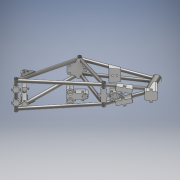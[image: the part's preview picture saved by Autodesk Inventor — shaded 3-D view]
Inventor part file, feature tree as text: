
AUTODESK INVENTOR PART (.ipt)
format: ipt  version: 2018 (Build 220112000, 112)  size: 1,251,840 bytes
history: native  units: mm
features: sketch x35, extrude x33, other x22, fillet x7, mirror x5, projected_geometry x5, plane x2, boolean_combine x2, loft x1, hole x1
ambient origin geometry x8: Origin, YZ Plane, XZ Plane, XY Plane, X Axis, Y Axis, Z Axis, Center Point
bodies: Solid1 (feature_tree), Solid2 (feature_tree), Solid3 (feature_tree), Solid16 (feature_tree), Solid17 (feature_tree), Solid21 (feature_tree)
feature tree (113):
  other  "MainFrame.ipt"
  other  "Floor"
  extrude  "Extrusion1"  Depth=10.0mm
  extrude  "Extrusion3"  Depth=18.25mm TaperAngle=0.0deg
  extrude  "Extrusion2"  Depth=4.0mm
  mirror  "Mirror1"
  extrude  "Extrusion5"  Depth=4.0mm TaperAngle=0.0deg
  extrude  "Extrusion6"  Depth=87.0mm TaperAngle=0.0deg
  extrude  "Extrusion7"  Depth=17.5mm TaperAngle=0.0deg
  extrude  "Extrusion8"  Depth=4.0mm
  extrude  "Extrusion9"  Depth=6.0mm TaperAngle=0.0deg
  extrude  "Extrusion10"  Depth=4.0mm
  extrude  "Extrusion11"  Depth=5.0mm TaperAngle=0.0deg
  extrude  "Extrusion12"  Depth=43.67578mm TaperAngle=0.0deg
  extrude  "Extrusion13"  TaperAngle=0.0deg  [1 undecoded]
  extrude  "Extrusion17"  Depth=4.0mm
  mirror  "Mirror3"
  extrude  "Extrusion35"  Depth=5.0mm TaperAngle=0.0deg
  extrude  "Extrusion45"  Depth=4.0mm
  mirror  "Mirror5"
  extrude  "Extrusion34"  Depth=10.0mm TaperAngle=0.0deg
  plane  "Work Plane22"
  extrude  "Extrusion19"  Depth=49.25mm TaperAngle=0.0deg
  plane  "Work Plane12"
  extrude  "Extrusion14"  Depth=116.0mm TaperAngle=0.0deg
  loft  "Loft1"
  extrude  "Extrusion15"  Depth=4.0mm
  extrude  "Extrusion16"  Depth=4.0mm TaperAngle=0.0deg
  mirror  "Mirror2"
  extrude  "Extrusion28"  Depth=22.0mm
  extrude  "Extrusion29"  Depth=10.0mm
  extrude  "Extrusion30"  Depth=5.0mm
  extrude  "Extrusion31"  Depth=11.1125mm
  extrude  "Extrusion32"  Depth=14.0mm
  extrude  "Extrusion33"  Depth=4.0mm
  fillet  "Fillet2"  Radius=57.75mm
  fillet  "Fillet3"  Radius=20.25mm
  boolean_combine  "Combine1"
  fillet  "Fillet5"  Radius=14.0mm
  fillet  "Fillet6"  Radius=17.75mm
  fillet  "Fillet7"  Radius=23.5mm
  extrude  "Extrusion36"  Depth=10.0mm TaperAngle=0.0deg
  mirror  "Mirror6"
  extrude  "Extrusion37"  [1 undecoded]
  extrude  "Extrusion38"  Depth=30.0mm
  boolean_combine  "Combine2"
  extrude  "Extrusion39"  Depth=10.0mm
  fillet  "Fillet8"  Radius=10.0mm
  hole  "Hole1"  [1 undecoded]
  extrude  "Extrusion41"  Depth=4.0mm
  extrude  "Extrusion42"  Depth=10.0mm TaperAngle=0.0deg
  fillet  "Fillet10"  Radius=6.0mm
  extrude  "Extrusion44"  Depth=6.0mm
  other  "Frame::MainFrame.ipt"
  other  "PivotPlateRight::MainFrame.ipt"
  other  "ShockPlateRight::MainFrame.ipt"
  other  "TaggingFeature1"
  sketch  "Sketch1"  dims[d0=10.0mm d1=18.0mm]
  other  "JigPartA"
  sketch  "Sketch2"  dims[d2=18.25mm d3=0.0mm d4=19.75mm d5=0.0mm]
  sketch  "Sketch3"  dims[d6=4.0mm d7=48.0mm]
  projected_geometry  "Projected Loop1"
  sketch  "Sketch6"  dims[d8=4.0mm d9=8.0mm d10=0.0mm]
  other  "JigPartB"
  sketch  "Sketch8"  dims[d13=87.0mm d14=0.0mm d15=87.0mm d16=0.0mm]
  sketch  "Sketch9"  dims[d17=87.0mm d18=0.0mm d19=17.5mm d20=0.0mm]
  sketch  "Sketch10"  dims[d21=17.5mm d22=0.0mm d23=4.0mm]
  sketch  "Sketch11"  dims[d24=4.0mm d25=6.0mm d26=0.0mm]
  other  "JigPartC"
  sketch  "Sketch12"  dims[d27=4.0mm d28=4.0mm]
  sketch  "Sketch13"  dims[d29=5.0mm d30=0.0mm d31=104.75mm d32=0.0mm]
  sketch  "Sketch14"  dims[d33=114.75mm d34=0.0mm d35=43.67578mm d36=0.0mm]
  other  "JigPartD-left"
  sketch  "Sketch15"  dims[d37=0.0mm d38=90.0deg d39=0.0mm d40=90.0deg]
  sketch  "Sketch16"  dims[d41=43.67578mm d42=0.0mm d43=4.0mm]
  other  "JigPartE"
  sketch  "Sketch17"  dims[d44=4.0mm d45=5.0mm d46=0.0mm]
  sketch  "Sketch18"  dims[d47=4.0mm d48=4.0mm]
  sketch  "Sketch19"  dims[d49=5.0mm d50=0.0mm d54=10.0mm d55=0.0mm]
  sketch  "Sketch20"  dims[d81=-185.0mm d82=49.25mm d83=0.0mm]
  sketch  "Sketch21"  dims[d84=116.0mm d85=0.0mm d86=116.0mm d87=0.0mm]
  sketch  "Sketch23"  dims[d88=9.8mm d89=40.0mm d90=0.0mm]
  other  "JigPartF-up"
  sketch  "Sketch32"  dims[d92=10.0mm d93=0.0mm d94=4.0mm]
  other  "JigPartG-up"
  sketch  "Sketch33"  dims[d95=4.0mm d96=4.0mm d97=0.0mm]
  sketch  "Sketch34"  dims[d98=22.0mm d103=20.0mm]
  sketch  "Sketch36"  dims[d104=10.0mm d105=0.0mm d106=38.1mm]
  other  "JigPartG-bottom"
  sketch  "Sketch39"  dims[d107=10.0mm d108=0.0mm d112=5.0mm]
  sketch  "Sketch42"  dims[d113=5.0mm d114=11.1125mm]
  other  "JigPartH"
  sketch  "Sketch43"  dims[d115=9.8mm d116=14.0mm]
  other  "JigPartI"
  other  "HeadTube::MainFrame.ipt"
  other  "PivotPlateLeft::MainFrame.ipt"
  projected_geometry  "Projected Loop6"
  sketch  "Sketch44"  dims[d117=11.5mm d118=4.0mm d120=57.75mm d121=20.25mm d122=14.0mm d123=17.75mm d124=0.0mm d125=23.5mm d126=0.0mm]
  sketch  "Sketch45"  dims[d128=23.5mm d129=0.0mm d130=10.0mm d131=0.0mm]
  sketch  "Sketch46"  dims[d132=14.0mm]
  sketch  "Sketch47"  dims[d133=9.8mm d134=6.0mm d135=4.0mm d136=2.0mm d137=90.0deg d138=8.0mm d139=20.594885mm d142=-243.5mm]
  sketch  "Sketch48"  dims[d143=40.0mm d144=0.0mm d146=30.0mm]
  sketch  "Sketch52"  dims[d147=30.0mm d148=30.0mm d149=10.0mm d150=0.0mm]
  other  "JigPartF-bottom"
  sketch  "Sketch54"  dims[d155=14.0mm d156=4.0mm]
  sketch  "Sketch56"  dims[d157=11.0mm d159=4.0mm]
  projected_geometry  "Projected Loop8"
  sketch  "Sketch57"  dims[d160=6.0mm d161=0.0mm d162=10.0mm d163=0.0mm d164=6.0mm d165=6.0mm d166=5.0mm d167=5.0mm]
  projected_geometry  "Projected Loop9"
  other  "Pattern of JigPartD-left:1"
  other  "JigPartD-right"
  other  "ShockPlateLeft::MainFrame.ipt"
  projected_geometry  "Project Cut Edges2"
note: 3 required parameter values undecoded (feature->parameter linkage not recoverable at this tier; creation-order binding heuristic only, values carry confidence <= 0.55)
